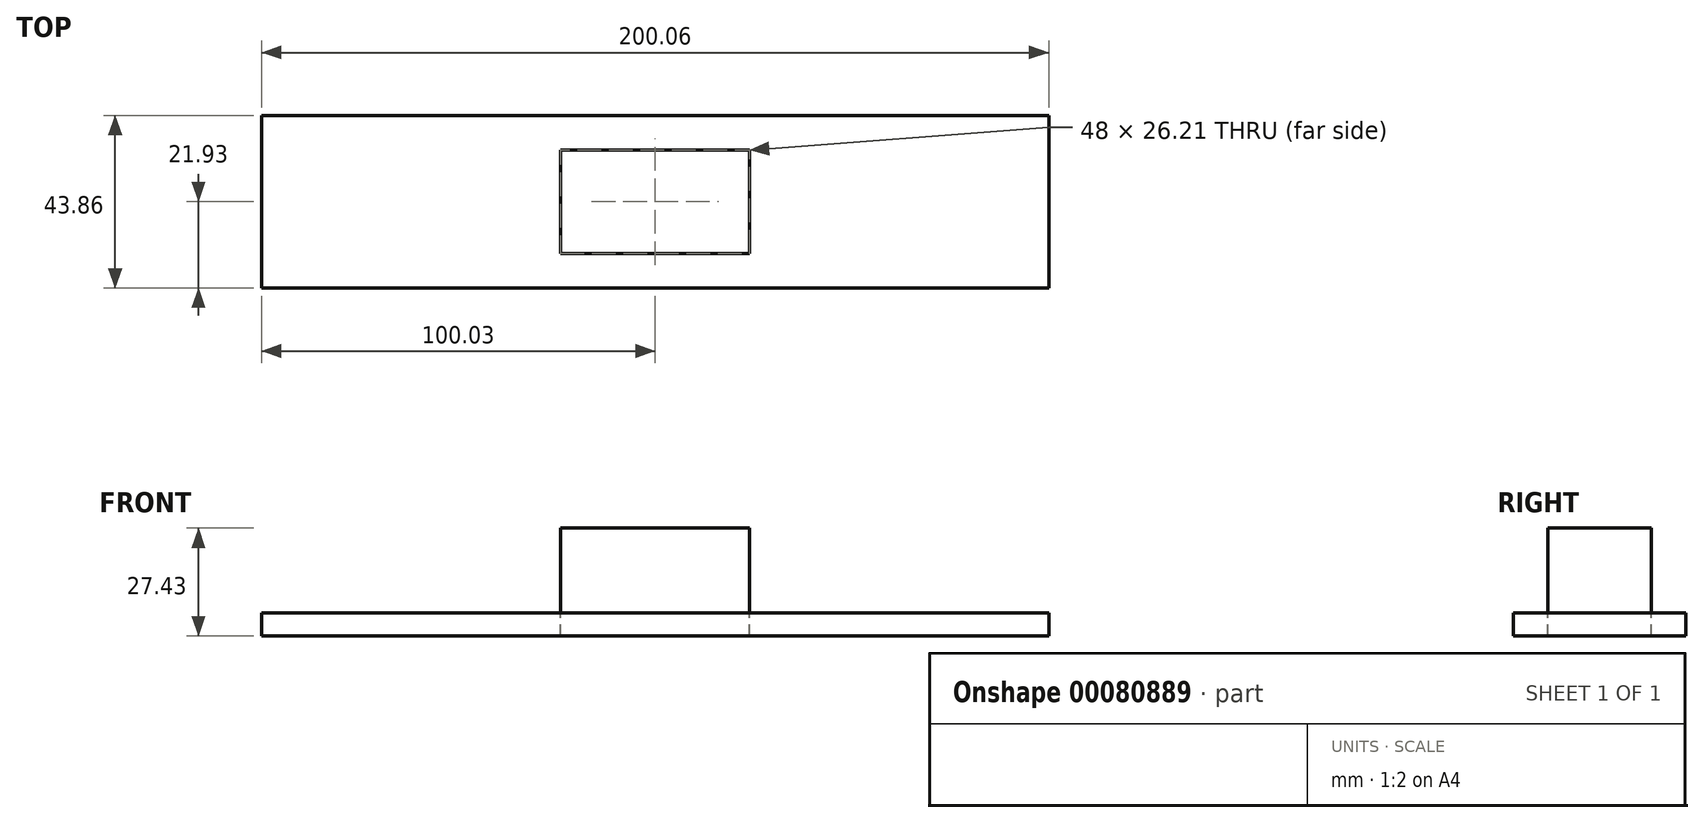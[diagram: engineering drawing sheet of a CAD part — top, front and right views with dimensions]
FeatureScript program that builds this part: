
annotation { "Feature Type Name" : "Feature", "Feature Type Description" : "" }
export const myFeature = defineFeature(function(context is Context, id is Id, definition is map)
    precondition{}
    {
        {
            var Q0;
            Q0=qCreatedBy(makeId("Top.planeOp"),FACE);
            var sketch = newSketch(context, id + "F0", { "sketchPlane" : qUnion([Q0])});
            skLineSegment(sketch, "E0.bottom", {"start": v(100.03, 21.93) * mm, "end": v(-100.03, 21.93) * mm});
            skLineSegment(sketch, "E0.top", {"start": v(100.03, -21.93) * mm, "end": v(-100.03, -21.93) * mm});
            skLineSegment(sketch, "E0.left", {"start": v(100.03, 21.93) * mm, "end": v(100.03, -21.93) * mm});
            skLineSegment(sketch, "E0.right", {"start": v(-100.03, 21.93) * mm, "end": v(-100.03, -21.93) * mm});
            skPoint(sketch, "E0.middle", {"position": v(0, 0) * mm});
            skLineSegment(sketch, "E1.bottom", {"start": v(24, -13.1) * mm, "end": v(-24, -13.1) * mm});
            skLineSegment(sketch, "E1.top", {"start": v(24, 13.1) * mm, "end": v(-24, 13.1) * mm});
            skLineSegment(sketch, "E1.left", {"start": v(24, -13.1) * mm, "end": v(24, 13.1) * mm});
            skLineSegment(sketch, "E1.right", {"start": v(-24, -13.1) * mm, "end": v(-24, 13.1) * mm});
            skSolve(sketch);
        }
        {
            var Q0;
            Q0=makeQuery(id+"F0.imprint","IMPRINT",FACE,{"disambiguationData":[TD([[makeQuery(id+"F0.imprint","IMPRINT",EDGE,{"derivedFrom":sQuery(id+"F0.wireOp",EDGE,"E1.bottom")}),-1.0]])]});
            extrude(context, id + "F1", {"entities" : qUnion([Q0]), "depth" : 21.59 * mm});
        }
        {
            var Q0;
            Q0=makeQuery(id+"F0.imprint","IMPRINT",FACE,{"disambiguationData":[TD([[makeQuery(id+"F0.imprint","IMPRINT",EDGE,{"derivedFrom":sQuery(id+"F0.wireOp",EDGE,"E0.bottom")}),1.0]])]});
            extrude(context, id + "F2", {"entities" : qUnion([Q0]), "oppositeDirection" : true, "depth" : 5.84 * mm});
        }
    });
